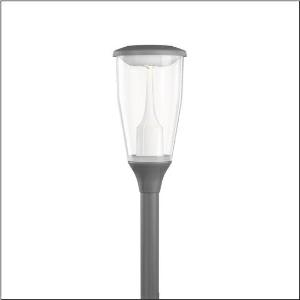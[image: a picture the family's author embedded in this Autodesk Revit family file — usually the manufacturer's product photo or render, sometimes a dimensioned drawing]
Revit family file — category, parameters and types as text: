
# Revit family: dl_11_iq___st1_2a_5xa5575af14h000022_aeb9
name_source: partatom
category: Lighting Fixtures
units: mm (PartAtom-declared; Revit-internal decimal feet)

## family parameters
Cut with Voids When Loaded = No
Host = Face
Light Source = No
Part Type = Normal
Room Calculation Point = No
Round Connector Dimension = Use Diameter
Shared = No

## types (1)
- --- (1 x LED, 1560 lm, 12.9 W, 2200K)
    Apparent Load = 13 VA
    CIE Flux Codes = 24 63 94 96 100
    Color Rendering = 70
    Color Temperature = 2200K
    Default Elevation = 1800 mm
    Description = DL 11 iQ, mast luminaire, Module 540 iQ-SR, primary light control with 3 zone facetted reflector, of plastic, silver coated, highly specular, structured, primary optical cover: cover, of PMMA, transparent, light distribution: ST1.2a, light emission: direct distribution, primary light characteristic: asymmetric, installation type: post-top, LED, High Power LED, rated luminous flux: 1.560lm, luminous efficacy: 149lm/W, light colour: 722, colour temperature: 2200K, control: Street-Remote, Auto-Match, Temp-Guard, Lumen-Switch, Night-Set, Smart-Wire, Light-Fading, Desk-Remote (wireless, voltage-free reading and setting of iQ features in the workshop via application-optimized NFC function/RFID function), optimised constant luminous flux control (CLO 2.0), mains connection: 220..240V, AC, 50/60Hz, connection cable pre-assembled, cable length: 5,5m, wiring characteristics: H07RN-F, 5-core, 1.5mm², start of lifetime: 13W, end of service life: 13W, reduction: 5W, luminaire housing, upper part, of diecast aluminium, coated, Siteco® metallic grey (DB 702S), spigot size: 76mm (post-top), post-top mast mounting element, of diecast aluminium, coated, Siteco® metallic grey (DB 702S), Module 540 iQ-SR, traffic white (RAL 9016), equipment: standard, protection rating (complete): IP66, insulation class (complete): insulation class II (safety insulation), certification: CE, ENEC, ENEC+, VDE, packaging unit: 1 piece

Light Distribution: ST1.2a
    Height = 665 mm
    Lamp = 1 x LED
    Lamp Light Flux = 1560 lm
    Lamp Power = 12.9 W
    Lamp count = 1
    Length = 334 mm
    Luminous efficacy = 121 lm/W
    Manufacturer = Siteco
    ModVariant = No
    Model = 5XA5575AF14H000022
    Number of Poles = 1
    OnlyDefault = Yes
    Power Factor = 1
    Product Name = DL 11 iQ | ST1.2a
    Product group = mast luminaire | pylon top
    ProductGroupID = 6100
    Protection Class = Protection class II
    Protection Degree = IP 66
    RLX_Detail_Level = 1
    RLX_Emergency_Light_Flux = 0 lm
    RLX_Emergency_Type = 0
    RLX_Emergency_Type_DB = No
    RlxData = <blob elided: 152385 chars, md5=ac4b4c68>
    Socket = socket
    Standby Power = 0 W
    System Light Flux = 1560 lm
    System Power = 13 W
    Type Comments = factory setting: luminous flux: 100 % | dim-lin: 254 | 516 mA
    Type Image = l_1258354.jpg
    URL = http://relux.com
    VarID = @adj_025805
    Voltage = 0 V
    Weight = 0.00 kg
    Width = 0 mm  [stored 0 ft]

note: [stored X ft] marks values corroborated as IEEE doubles in the binary element streams (Revit-internal decimal feet)

## geometry (parser evidence)
native form markers: Blend x4, Sweep x11
no freeform markers — native parametric forms only
